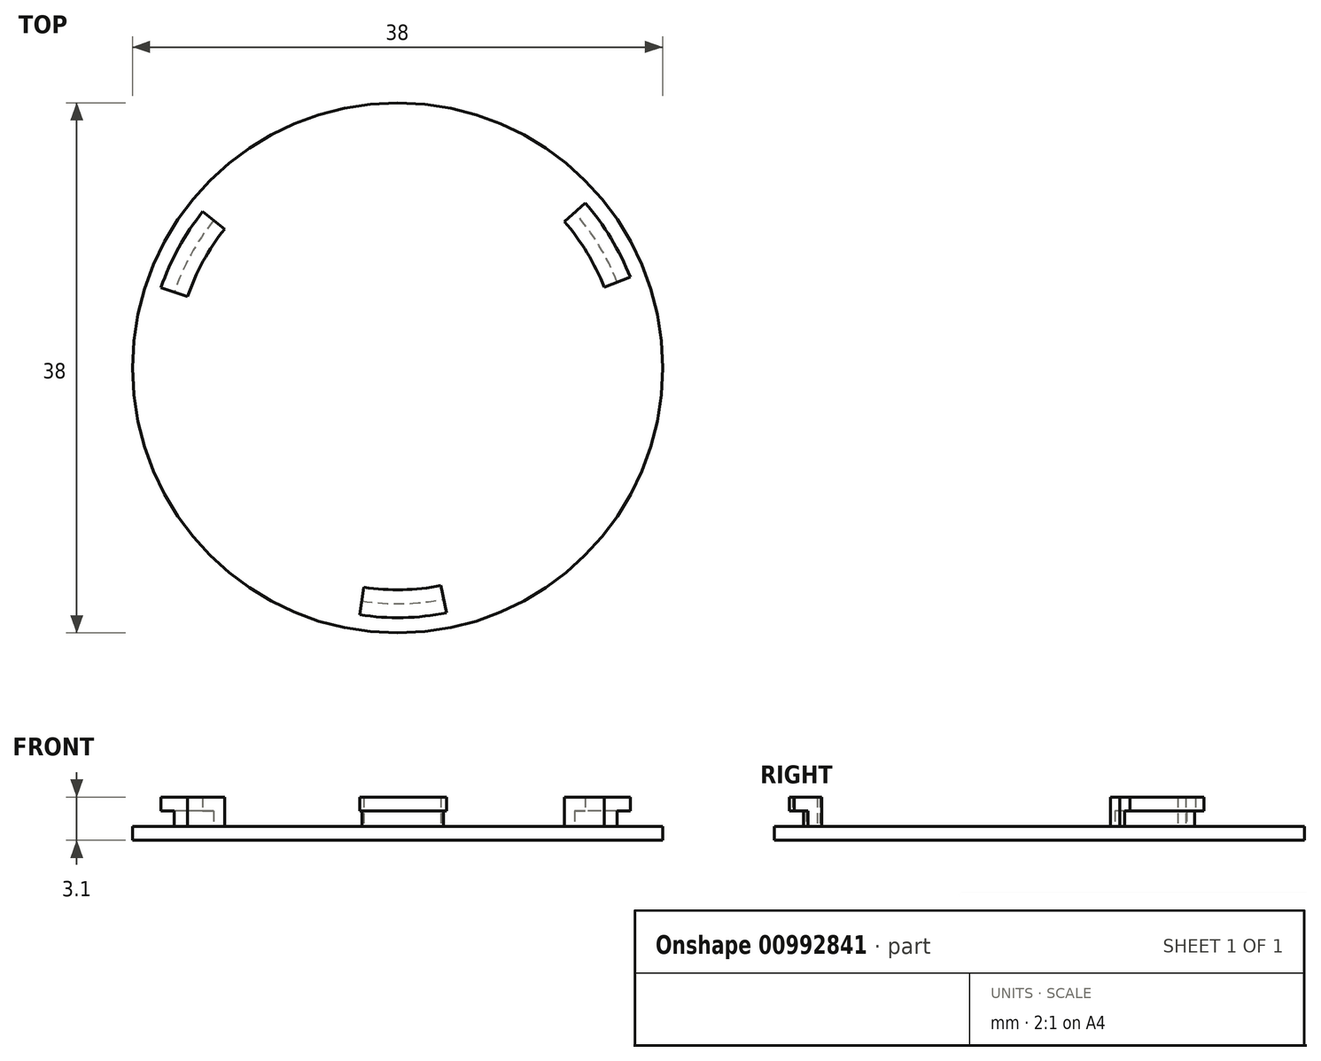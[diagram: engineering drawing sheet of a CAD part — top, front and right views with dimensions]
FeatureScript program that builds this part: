
annotation { "Feature Type Name" : "Feature", "Feature Type Description" : "" }
export const myFeature = defineFeature(function(context is Context, id is Id, definition is map)
    precondition{}
    {
        {
            var Q0;
            Q0=qCreatedBy(makeId("Top.planeOp"),FACE);
            var sketch = newSketch(context, id + "F0", { "sketchPlane" : qUnion([Q0])});
            skCircle(sketch, "E0", {"center": v(0, 0) * mm, "radius": 19 * mm});
            skSolve(sketch);
        }
        {
            var Q0;
            Q0 = qSketchRegion(id + "F0", true);
            extrude(context, id + "F1", {"entities" : qUnion([Q0]), "depth" : 1 * mm, "offsetDistance" : 25.4 * mm});
        }
        {
            var Q0;
            Q0=makeQuery(id+"F1.opExtrude","CAP_FACE",FACE,{"disambiguationData":[OSD([sQuery(id+"F0.wireOp",EDGE,"E0")])],"isStart":false});
            var sketch = newSketch(context, id + "F2", { "sketchPlane" : qUnion([Q0])});
            skArc(sketch, "E1", {"start": v(15.75, 6.13) * mm, "mid": v(14.44, 8.78) * mm, "end": v(12.7, 11.15) * mm});
            skLineSegment(sketch, "E2", {"start": v(12.7, 11.15) * mm, "end": v(0, 0) * mm, "construction": true});
            skLineSegment(sketch, "E3", {"start": v(0, 0) * mm, "end": v(15.75, 6.13) * mm, "construction": true});
            skLineSegment(sketch, "E4", {"start": v(12.7, 11.15) * mm, "end": v(11.95, 10.5) * mm});
            skLineSegment(sketch, "E5", {"start": v(15.75, 6.13) * mm, "end": v(14.82, 5.77) * mm});
            skArc(sketch, "E6", {"start": v(14.82, 5.77) * mm, "mid": v(13.59, 8.26) * mm, "end": v(11.95, 10.5) * mm});
            skArc(sketch, "E7.1.0", {"start": v(-12.4, 9.95) * mm, "mid": v(-13.94, 7.64) * mm, "end": v(-15.06, 5.1) * mm});
            skArc(sketch, "E7.1.1", {"start": v(-13.19, 10.57) * mm, "mid": v(-14.82, 8.12) * mm, "end": v(-16, 5.42) * mm});
            skLineSegment(sketch, "E7.1.2", {"start": v(-16, 5.42) * mm, "end": v(-15.06, 5.1) * mm});
            skLineSegment(sketch, "E7.1.3", {"start": v(-13.19, 10.57) * mm, "end": v(-12.4, 9.95) * mm});
            skArc(sketch, "E7.2.0", {"start": v(-2.41, -15.72) * mm, "mid": v(0.36, -15.9) * mm, "end": v(3.11, -15.6) * mm});
            skArc(sketch, "E7.2.1", {"start": v(-2.56, -16.7) * mm, "mid": v(0.38, -16.9) * mm, "end": v(3.3, -16.57) * mm});
            skLineSegment(sketch, "E7.2.2", {"start": v(3.3, -16.57) * mm, "end": v(3.11, -15.6) * mm});
            skLineSegment(sketch, "E7.2.3", {"start": v(-2.56, -16.7) * mm, "end": v(-2.41, -15.72) * mm});
            skSolve(sketch);
        }
        {
            var Q0;
            Q0 = qSketchRegion(id + "F2", true);
            extrude(context, id + "F3", {"entities" : qUnion([Q0]), "operationType" : NewBodyOperationType.ADD, "depth" : 1.1 * mm, "offsetDistance" : 25.4 * mm});
        }
        {
            var Q0;
            Q0=makeQuery(id+"F3.opExtrude","CAP_FACE",FACE,{"disambiguationData":[OSD([sQuery(id+"F2.wireOp",EDGE,"E7.1.0"),sQuery(id+"F2.wireOp",EDGE,"E7.1.1"),sQuery(id+"F2.wireOp",EDGE,"E7.1.2"),sQuery(id+"F2.wireOp",EDGE,"E7.1.3")])],"isStart":false});
            var sketch = newSketch(context, id + "F4", { "sketchPlane" : qUnion([Q0])});
            skLineSegment(sketch, "E8.0", {"start": v(-13.19, 10.57) * mm, "end": v(-12.4, 9.95) * mm, "construction": true});
            skArc(sketch, "E9.0", {"start": v(-13.19, 10.57) * mm, "mid": v(-14.82, 8.12) * mm, "end": v(-16, 5.42) * mm, "construction": true});
            skLineSegment(sketch, "E10.0", {"start": v(-16, 5.42) * mm, "end": v(-15.06, 5.1) * mm, "construction": true});
            skLineSegment(sketch, "E11", {"start": v(-12.4, 9.95) * mm, "end": v(-13.97, 11.2) * mm});
            skLineSegment(sketch, "E12", {"start": v(-15.06, 5.1) * mm, "end": v(-16.95, 5.74) * mm});
            skArc(sketch, "E13", {"start": v(-13.97, 11.2) * mm, "mid": v(-15.7, 8.6) * mm, "end": v(-16.95, 5.74) * mm});
            skArc(sketch, "E14.0", {"start": v(-12.4, 9.95) * mm, "mid": v(-13.94, 7.64) * mm, "end": v(-15.06, 5.1) * mm});
            skArc(sketch, "E15.1.0", {"start": v(-2.71, -17.7) * mm, "mid": v(0.4, -17.9) * mm, "end": v(3.5, -17.55) * mm});
            skLineSegment(sketch, "E15.1.1", {"start": v(-2.41, -15.72) * mm, "end": v(-2.71, -17.7) * mm});
            skLineSegment(sketch, "E15.1.2", {"start": v(3.11, -15.6) * mm, "end": v(3.5, -17.55) * mm});
            skArc(sketch, "E15.1.3", {"start": v(-2.41, -15.72) * mm, "mid": v(0.36, -15.9) * mm, "end": v(3.11, -15.6) * mm});
            skArc(sketch, "E15.2.0", {"start": v(16.68, 6.5) * mm, "mid": v(15.3, 9.3) * mm, "end": v(13.45, 11.8) * mm});
            skLineSegment(sketch, "E15.2.1", {"start": v(14.82, 5.77) * mm, "end": v(16.68, 6.5) * mm});
            skLineSegment(sketch, "E15.2.2", {"start": v(11.95, 10.5) * mm, "end": v(13.45, 11.8) * mm});
            skArc(sketch, "E15.2.3", {"start": v(14.82, 5.77) * mm, "mid": v(13.59, 8.26) * mm, "end": v(11.95, 10.5) * mm});
            skLineSegment(sketch, "E16", {"start": v(-13.94, 7.64) * mm, "end": v(0, 0) * mm, "construction": true});
            skSolve(sketch);
        }
        {
            var Q0;
            Q0 = qSketchRegion(id + "F4", true);
            extrude(context, id + "F5", {"entities" : qUnion([Q0]), "operationType" : NewBodyOperationType.ADD, "depth" : 1 * mm, "offsetDistance" : 25.4 * mm});
        }
    });
